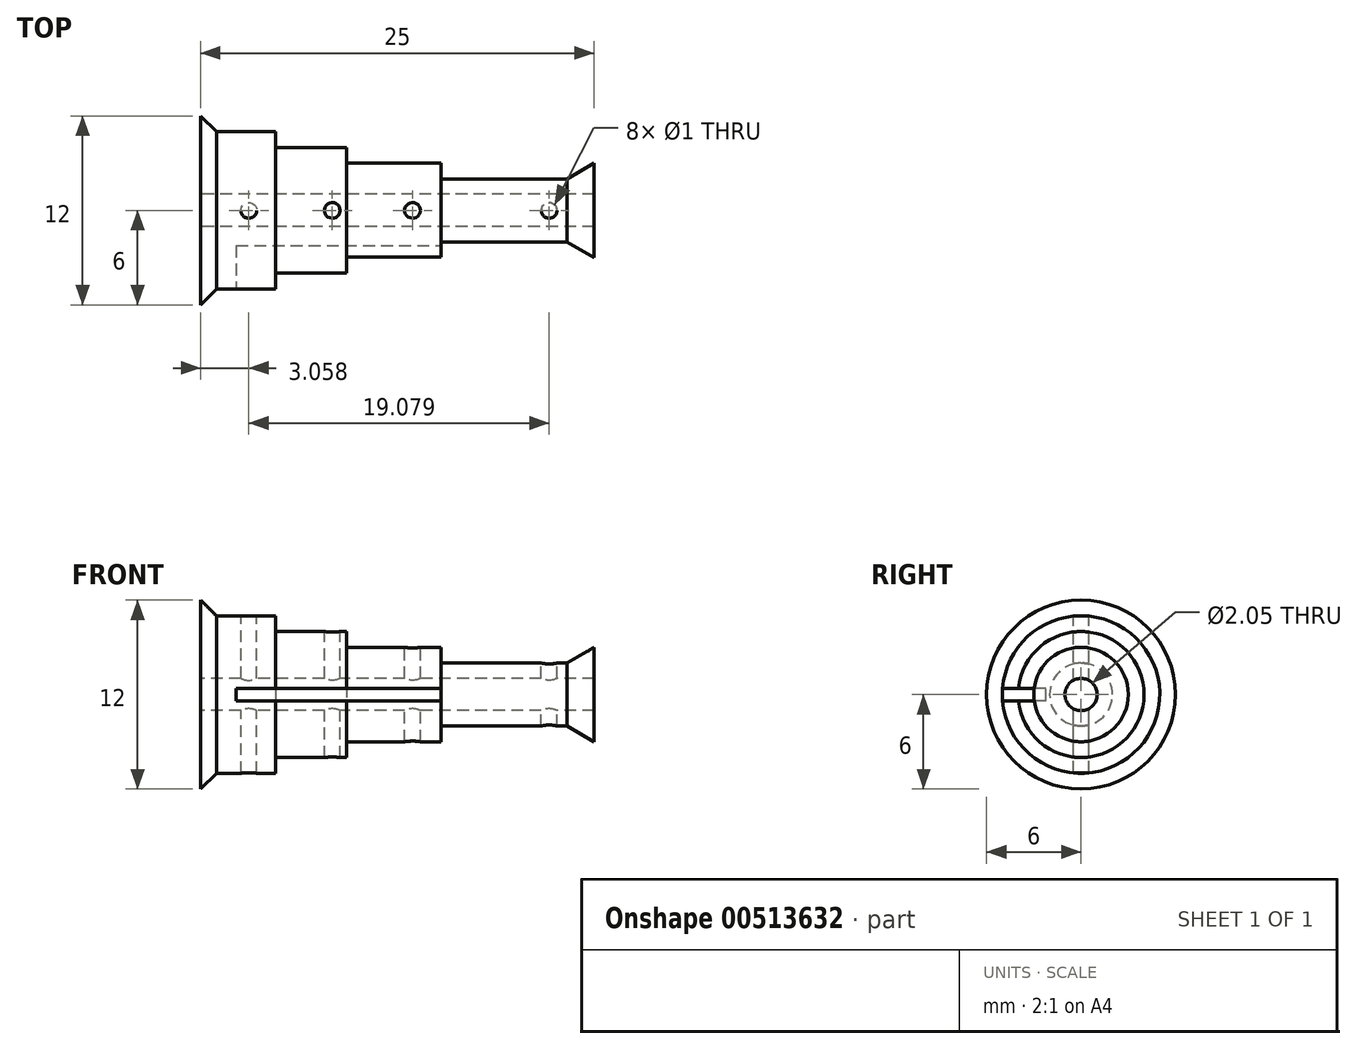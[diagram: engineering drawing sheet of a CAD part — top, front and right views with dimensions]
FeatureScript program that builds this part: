
annotation { "Feature Type Name" : "Feature", "Feature Type Description" : "" }
export const myFeature = defineFeature(function(context is Context, id is Id, definition is map)
    precondition{}
    {
        {
            var Q0;
            Q0=qCreatedBy(makeId("Front.planeOp"),FACE);
            var sketch = newSketch(context, id + "F0", { "sketchPlane" : qUnion([Q0])});
            skLineSegment(sketch, "E0", {"start": v(-22.67, 0) * mm, "end": v(34.76, 0) * mm, "construction": true});
            skLineSegment(sketch, "E1", {"start": v(0, 6) * mm, "end": v(0, 0) * mm});
            skLineSegment(sketch, "E2", {"start": v(0, 0) * mm, "end": v(0, 6) * mm});
            skLineSegment(sketch, "E3", {"start": v(25, 3) * mm, "end": v(25, 0) * mm});
            skLineSegment(sketch, "E4", {"start": v(0, 1.02) * mm, "end": v(25, 1.02) * mm});
            skLineSegment(sketch, "E5", {"start": v(23.27, 2) * mm, "end": v(25, 3) * mm});
            skLineSegment(sketch, "E6", {"start": v(25, 3) * mm, "end": v(25, 3) * mm});
            skLineSegment(sketch, "E7", {"start": v(1, 5) * mm, "end": v(4.77, 5) * mm});
            skLineSegment(sketch, "E8", {"start": v(15.27, 2) * mm, "end": v(23.27, 2) * mm});
            skLineSegment(sketch, "E9", {"start": v(1, 5) * mm, "end": v(0, 6) * mm});
            skLineSegment(sketch, "E10", {"start": v(4.77, 5) * mm, "end": v(4.77, 4) * mm});
            skLineSegment(sketch, "E11", {"start": v(4.77, 4) * mm, "end": v(9.27, 4) * mm});
            skLineSegment(sketch, "E12", {"start": v(9.27, 4) * mm, "end": v(9.27, 3) * mm});
            skLineSegment(sketch, "E13", {"start": v(9.27, 3) * mm, "end": v(15.27, 3) * mm});
            skLineSegment(sketch, "E14", {"start": v(15.27, 3) * mm, "end": v(15.27, 2) * mm});
            skSolve(sketch);
        }
        {
            var Q0;
            Q0=qSketchRegion(id+"F0",true);
            var Q1;
            Q1=sQuery(id+"F0.wireOp",EDGE,"E0");
            revolve(context, id + "F1", {"entities" : qUnion([Q0]), "axis" : qUnion([Q1]), "revolveType" : RevolveType.FULL});
        }
        {
            var Q0;
            Q0=qCreatedBy(makeId("Top.planeOp"),FACE);
            var sketch = newSketch(context, id + "F2", { "sketchPlane" : qUnion([Q0])});
            skCircle(sketch, "E15", {"center": v(3.06, 0) * mm, "radius": 0.5 * mm});
            skCircle(sketch, "E16", {"center": v(8.36, 0) * mm, "radius": 0.5 * mm});
            skCircle(sketch, "E17", {"center": v(13.46, 0) * mm, "radius": 0.5 * mm});
            skCircle(sketch, "E18", {"center": v(22.14, 0) * mm, "radius": 0.5 * mm});
            skSolve(sketch);
        }
        {
            var Q0;
            Q0=qSketchRegion(id+"F2",true);
            extrude(context, id + "F3", {"entities" : qUnion([Q0]), "operationType" : NewBodyOperationType.REMOVE, "endBound" : BoundingType.SYMMETRIC, "oppositeDirection" : true, "depth" : 25 * mm, "offsetDistance" : 25 * mm});
        }
        {
            var Q0;
            Q0=makeQuery(id+"F1.opRevolve","SWEPT_FACE",FACE,{"disambiguationData":[OSD([sQuery(id+"F0.wireOp",EDGE,"E14")])]});
            var sketch = newSketch(context, id + "F4", { "sketchPlane" : qUnion([Q0])});
            skLineSegment(sketch, "E19", {"start": v(-3, 0) * mm, "end": v(-4.2, 0) * mm, "construction": true});
            skLineSegment(sketch, "E20.bottom", {"start": v(-2.23, -0.4) * mm, "end": v(-5.02, -0.4) * mm});
            skLineSegment(sketch, "E20.top", {"start": v(-2.23, 0.4) * mm, "end": v(-5.02, 0.4) * mm});
            skLineSegment(sketch, "E20.right", {"start": v(-5.02, -0.4) * mm, "end": v(-5.02, 0.4) * mm});
            skLineSegment(sketch, "E21", {"start": v(-2.23, -0.4) * mm, "end": v(-2.23, 0.4) * mm});
            skSolve(sketch);
        }
        {
            var Q0;
            Q0 = qSketchRegion(id + "F4", true);
            extrude(context, id + "F5", {"entities" : qUnion([Q0]), "operationType" : NewBodyOperationType.REMOVE, "oppositeDirection" : true, "depth" : 13 * mm, "offsetDistance" : 25 * mm});
        }
    });
